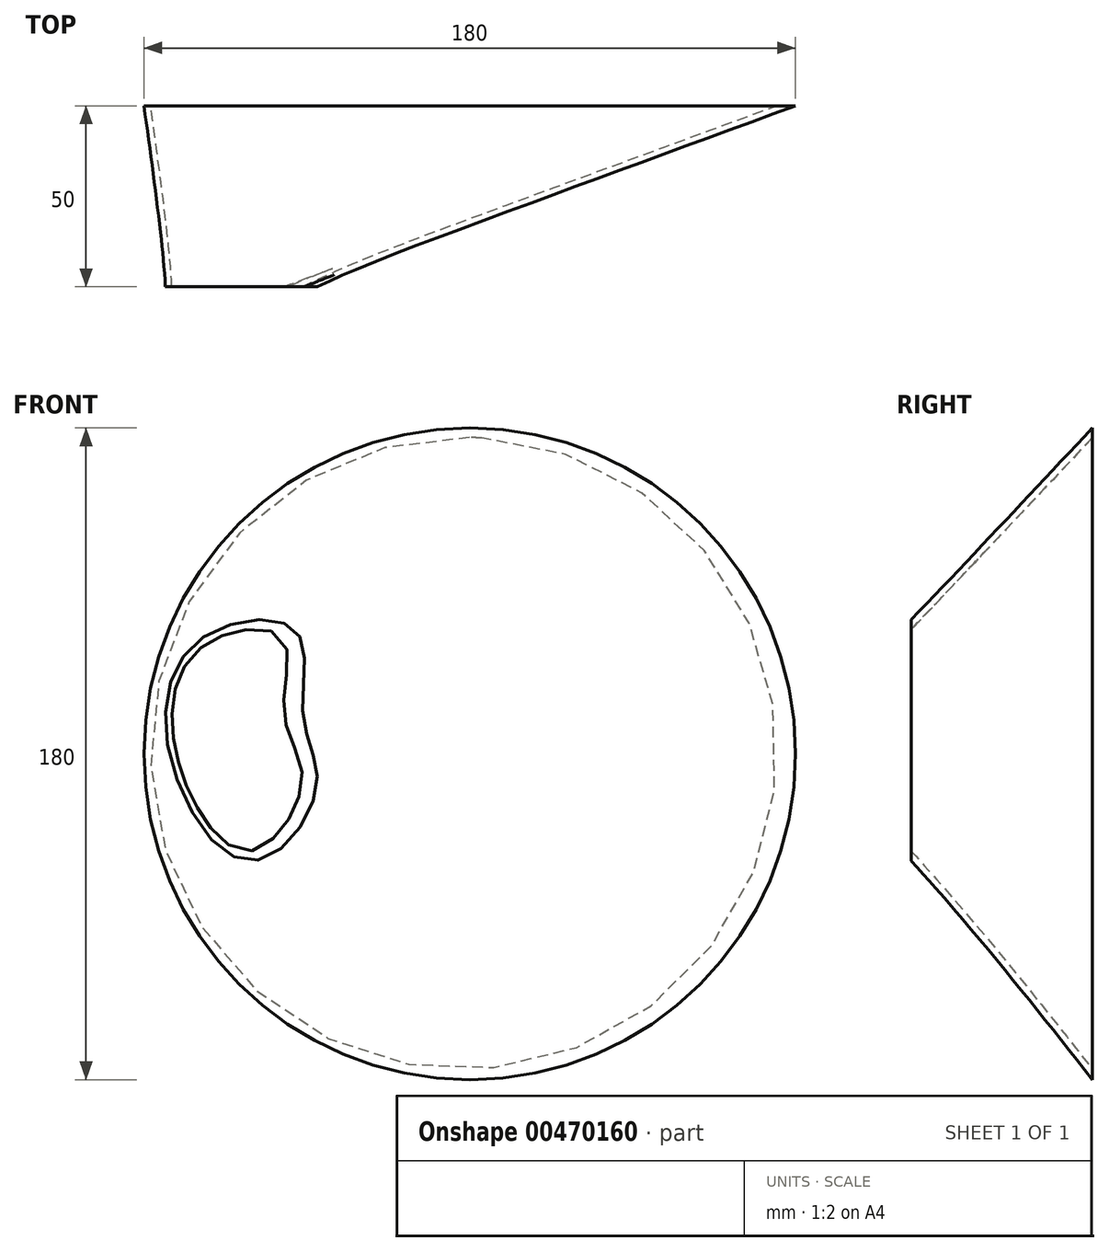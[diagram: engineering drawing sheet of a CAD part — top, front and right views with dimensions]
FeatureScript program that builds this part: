
annotation { "Feature Type Name" : "Feature", "Feature Type Description" : "" }
export const myFeature = defineFeature(function(context is Context, id is Id, definition is map)
    precondition{}
    {
        {
            var Q0;
            Q0=qCreatedBy(makeId("Front.planeOp"),FACE);
            var sketch = newSketch(context, id + "F0", { "sketchPlane" : qUnion([Q0])});
            skCircle(sketch, "E0", {"center": v(0, 0) * mm, "radius": 90 * mm});
            skSolve(sketch);
        }
        {
            var Q0;
            Q0=qCreatedBy(makeId("Front.planeOp"),FACE);
            cPlane(context, id + "F1", {"entities" : qUnion([Q0]), "cplaneType" : CPlaneType.OFFSET, "offset" : 50 * mm, "width" : 150 * mm, "height" : 150 * mm});
        }
        {
            var Q0;
            Q0=qCreatedBy(id+"F1.planeOp",FACE);
            var sketch = newSketch(context, id + "F2", { "sketchPlane" : qUnion([Q0])});
            skFitSpline(sketch, "E1", {"points": [v(-82.97, 0) * mm, v(-73.94, 31.98) * mm, v(-48.02, 33.88) * mm, v(-46.12, 10.58) * mm, v(-42.32, -9.4) * mm, v(-60.38, -29.6) * mm, v(-82.97, 0) * mm]});
            skSolve(sketch);
        }
        {
            var Q0;
            Q0=makeQuery(id+"F0.imprint","IMPRINT",FACE,{"disambiguationData":[TD([[makeQuery(id+"F0.imprint","IMPRINT",EDGE,{"derivedFrom":sQuery(id+"F0.wireOp",EDGE,"E0")}),1.0]])]});
            var Q1;
            Q1=makeQuery(id+"F2.imprint","IMPRINT",FACE,{"disambiguationData":[TD([[makeQuery(id+"F2.imprint","IMPRINT",EDGE,{"derivedFrom":sQuery(id+"F2.wireOp",EDGE,"E1")}),-1.0]])]});
            loft(context, id + "F3", {"sheetProfilesArray" : [{ "sheetProfileEntities" : qUnion([Q0]) }, { "sheetProfileEntities" : qUnion([Q1]) }]});
        }
        {
            var Q0;
            Q0=makeQuery(id+"F3.opLoft","CAP_FACE",FACE,{"disambiguationData":[OSD([makeQuery(id+"F2.imprint","IMPRINT",FACE,{"disambiguationData":[TD([[makeQuery(id+"F2.imprint","IMPRINT",EDGE,{"derivedFrom":sQuery(id+"F2.wireOp",EDGE,"E1")}),-1.0]])]})])],"isStart":true});
            var Q1;
            Q1=makeQuery(id+"F3.opLoft","CAP_FACE",FACE,{"disambiguationData":[OSD([makeQuery(id+"F0.imprint","IMPRINT",FACE,{"disambiguationData":[TD([[makeQuery(id+"F0.imprint","IMPRINT",EDGE,{"derivedFrom":sQuery(id+"F0.wireOp",EDGE,"E0")}),1.0]])]})])],"isStart":true});
            shell(context, id + "F4", {"entities" : qUnion([Q0, Q1]), "thickness" : 1.8 * mm});
        }
    });
